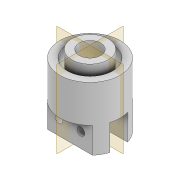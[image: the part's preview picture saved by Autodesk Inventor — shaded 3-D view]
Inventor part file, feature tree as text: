
AUTODESK INVENTOR PART (.ipt)
format: ipt  version: 2022 (Build 260153000, 153)  size: 153,088 bytes
history: native  units: mm
features: extrude x5, sketch x4, projected_geometry x1
ambient origin geometry x8: Origin, YZ Plane, XZ Plane, XY Plane, X Axis, Y Axis, Z Axis, Center Point
bodies: Solid1 (feature_tree)
feature tree (10):
  sketch  "Sketch1"  dims[d0=12.2mm d1=9.8mm]
  extrude  "Extrusion1"  Depth=9.8mm
  extrude  "Extrusion2"  Depth=3.0mm TaperAngle=0.0deg
  extrude  "Extrusion7"  Depth=10.0mm TaperAngle=0.0deg
  extrude  "Extrusion8"  Depth=3.0mm
  extrude  "Extrusion9"  Depth=4.8mm
  sketch  "Sketch7"  dims[d2=2.0mm d3=3.0mm d4=0.0mm]
  sketch  "Sketch8"  dims[d5=2.0mm d6=10.0mm d7=0.0mm]
  sketch  "Sketch9"  dims[d34=3.0mm d35=3.0mm d36=4.8mm d37=2.4mm d38=7.0mm d39=0.0mm d40=2.1mm d41=2.1mm d42=3.0mm d43=3.0mm d44=5.9mm d45=2.95mm d46=20.0mm d47=0.0mm d48=2.0mm d49=0.0mm d27=0.0mm d28=0.0mm d29=0.0mm d30=0.0mm]
  projected_geometry  "Project Cut Edges1"
